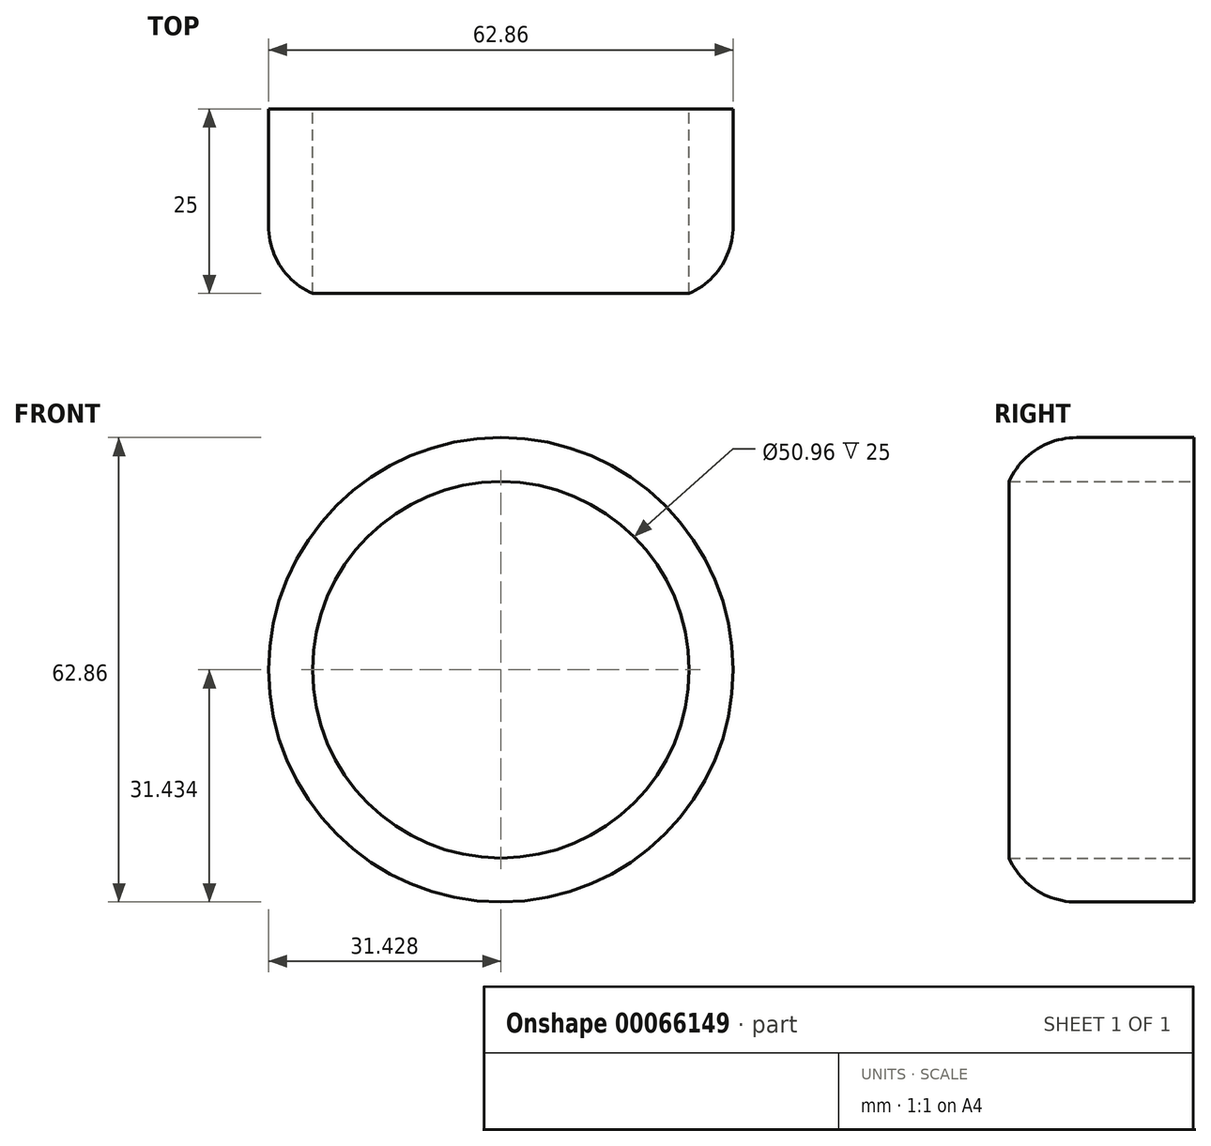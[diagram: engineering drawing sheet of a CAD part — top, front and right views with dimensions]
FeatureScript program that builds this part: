
annotation { "Feature Type Name" : "Feature", "Feature Type Description" : "" }
export const myFeature = defineFeature(function(context is Context, id is Id, definition is map)
    precondition{}
    {
        {
            var Q0;
            Q0=qCreatedBy(makeId("Front.planeOp"),FACE);
            var sketch = newSketch(context, id + "F0", { "sketchPlane" : qUnion([Q0])});
            skCircle(sketch, "E0", {"center": v(-35.23, 27.87) * mm, "radius": 31.43 * mm});
            skCircle(sketch, "E1", {"center": v(-35.23, 27.87) * mm, "radius": 25.48 * mm});
            skSolve(sketch);
        }
        {
            var Q0;
            Q0 = qSketchRegion(id + "F0", true);
            extrude(context, id + "F1", {"entities" : qUnion([Q0]), "depth" : 25 * mm});
        }
        {
            var Q0;
            Q0=makeQuery(id+"F1.opExtrude","CAP_EDGE",EDGE,{"disambiguationData":[OSD([sQuery(id+"F0.wireOp",EDGE,"E0")])],"isStart":false});
            fillet(context, id + "F2", {"entities" : qUnion([Q0]), "radius" : 10 * mm, "tangentPropagation" : true, "allowEdgeOverflow" : false});
        }
    });
